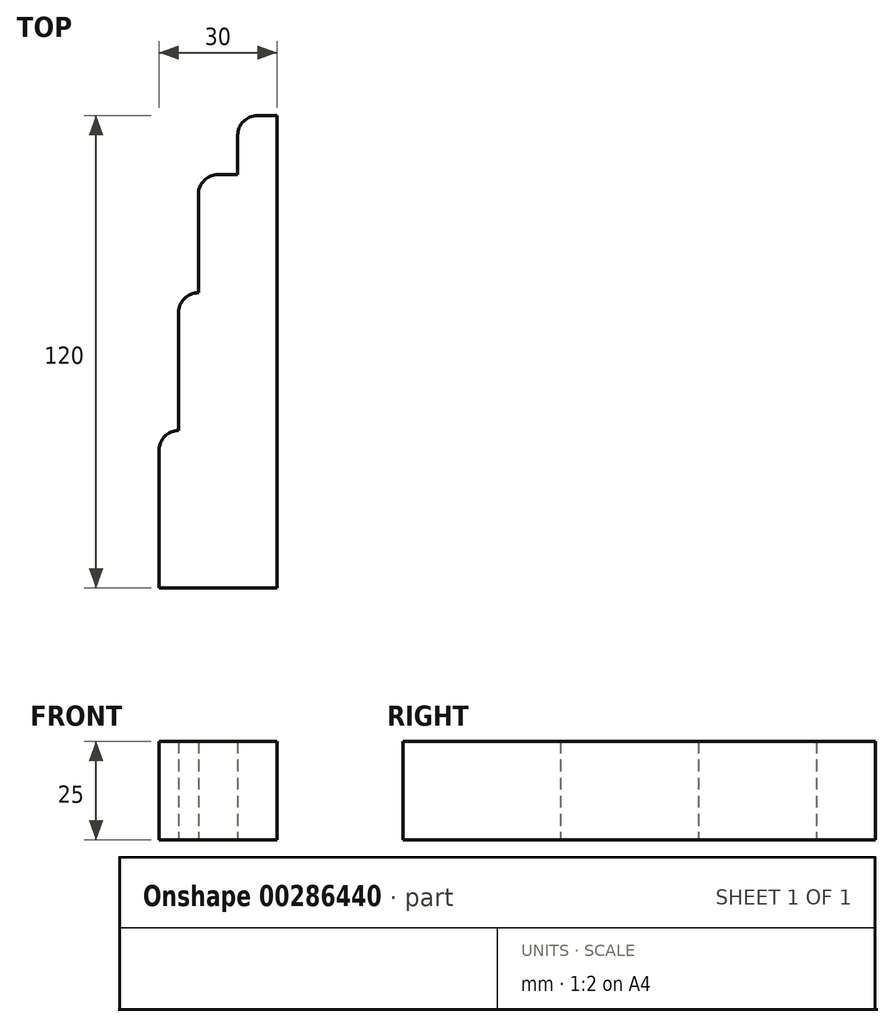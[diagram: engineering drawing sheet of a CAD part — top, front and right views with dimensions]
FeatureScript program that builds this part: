
annotation { "Feature Type Name" : "Feature", "Feature Type Description" : "" }
export const myFeature = defineFeature(function(context is Context, id is Id, definition is map)
    precondition{}
    {
        {
            var Q0;
            Q0=qCreatedBy(makeId("Top.planeOp"),FACE);
            var sketch = newSketch(context, id + "F0", { "sketchPlane" : qUnion([Q0])});
            skLineSegment(sketch, "E0", {"start": v(-36.49, -82.77) * mm, "end": v(-6.49, -82.77) * mm});
            skLineSegment(sketch, "E1", {"start": v(-6.49, -82.77) * mm, "end": v(-6.49, 37.23) * mm});
            skLineSegment(sketch, "E2", {"start": v(-6.49, 37.23) * mm, "end": v(-11.49, 37.23) * mm});
            skLineSegment(sketch, "E3", {"start": v(-16.49, 32.23) * mm, "end": v(-16.49, 22.23) * mm});
            skLineSegment(sketch, "E4", {"start": v(-16.49, 22.23) * mm, "end": v(-21.49, 22.23) * mm});
            skLineSegment(sketch, "E5", {"start": v(-26.49, 17.23) * mm, "end": v(-26.49, -7.77) * mm});
            skLineSegment(sketch, "E6", {"start": v(-26.49, -7.77) * mm, "end": v(-26.49, -7.77) * mm});
            skLineSegment(sketch, "E7", {"start": v(-31.49, -12.77) * mm, "end": v(-31.49, -42.77) * mm});
            skLineSegment(sketch, "E8", {"start": v(-31.49, -42.77) * mm, "end": v(-31.49, -42.77) * mm});
            skLineSegment(sketch, "E9", {"start": v(-36.49, -47.77) * mm, "end": v(-36.49, -82.77) * mm});
            skPoint(sketch, "E10.visualSharp", {"position": v(-36.49, -42.77) * mm});
            skArc(sketch, "E10.filletArc", {"start": v(-31.49, -42.77) * mm, "mid": v(-35.02, -44.23) * mm, "end": v(-36.49, -47.77) * mm});
            skPoint(sketch, "E11.visualSharp", {"position": v(-31.49, -7.77) * mm});
            skArc(sketch, "E11.filletArc", {"start": v(-26.49, -7.77) * mm, "mid": v(-30.02, -9.23) * mm, "end": v(-31.49, -12.77) * mm});
            skPoint(sketch, "E12.visualSharp", {"position": v(-26.49, 22.23) * mm});
            skArc(sketch, "E12.filletArc", {"start": v(-21.49, 22.23) * mm, "mid": v(-25.02, 20.77) * mm, "end": v(-26.49, 17.23) * mm});
            skPoint(sketch, "E13.visualSharp", {"position": v(-16.49, 37.23) * mm});
            skArc(sketch, "E13.filletArc", {"start": v(-11.49, 37.23) * mm, "mid": v(-15.02, 35.77) * mm, "end": v(-16.49, 32.23) * mm});
            skSolve(sketch);
        }
        {
            var Q0;
            Q0=makeQuery(id+"F0.imprint","IMPRINT",FACE,{"disambiguationData":[TD([[makeQuery(id+"F0.imprint","IMPRINT",EDGE,{"derivedFrom":sQuery(id+"F0.wireOp",EDGE,"E0")}),1.0]])]});
            extrude(context, id + "F1", {"entities" : qUnion([Q0]), "depth" : 25 * mm});
        }
    });
